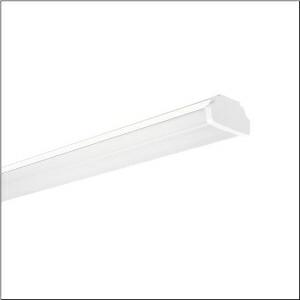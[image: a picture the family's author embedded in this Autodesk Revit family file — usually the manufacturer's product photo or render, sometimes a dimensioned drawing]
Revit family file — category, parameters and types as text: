
# Revit family: modario_r__31_ho_53bm812d2v4120_42ed
name_source: partatom
category: Lighting Fixtures
units: mm (PartAtom-declared; Revit-internal decimal feet)

## family parameters
Cut with Voids When Loaded = No
Host = Face
Light Source = No
Part Type = Normal
Room Calculation Point = No
Round Connector Dimension = Use Diameter
Shared = No

## types (1)
- --- (1 x LED, 12350 lm, 79.5 W, 4000K)
    Apparent Load = 80 VA
    CIE Flux Codes = 47 80 95 92 100
    Color Rendering = 80
    Color Temperature = 4000K
    Default Elevation = 1800 mm
    Description = Modario® 31 HO, luminaire insert, of sheet steel, coil coated, white, length: 1.495mm, width: 81mm, height: 82mm, 5x system unit, system units: 299mm, LED rated luminous flux: 12.350lm, light colour: 840, control gear: DALI 2, control gear: ECG DALI, with plug, 5-pole, with phase selection, mains connection: 220..240V, AC, 50/60Hz, rated input power: 80W, through-wiring accessed according to module size, primary optical cover: cover, of PMMA, light emission: direct distribution, primary light characteristic: symmetric, protection rating (complete): IP20, protection rating (LED compartment): IP50, insulation class (complete): insulation class I (protective earthing), certification: CE, ENEC, VDE, UKCA, impact resistance: IK03, permissible ambient temperature for indoor applications: -25..+30°C, corresponds to IFS (International Featured Standards) requirements for safety and quality in the food industry, reducing of maximum allowable ambient temperature of 5°C with ceiling mounting, packaging unit: 1 piece
    Height = 92 mm
    Lamp = 1 x LED
    Lamp Light Flux = 12350 lm
    Lamp Power = 79.5 W
    Lamp count = 1
    Length = 1495 mm
    Luminous efficacy = 155 lm/W
    Manufacturer = Siteco
    ModVariant = No
    Model = 53BM812D2V4120
    Mounting Place = Ceiling
    Mounting Type = Pendant
    Number of Poles = 1
    OnlyDefault = Yes
    Power Factor = 1
    Product Name = Modario® 31 HO
    Product group = luminaire insert
    ProductGroupID = 902
    Protection Class = Protection class I
    Protection Degree = IP 20
    RLX_Detail_Level = 1
    RLX_Emergency_Light_Flux = 0 lm
    RLX_Emergency_Type = 0
    RLX_Emergency_Type_DB = No
    RlxData = <blob elided: 42261 chars, md5=d68db8b3>
    Socket = socket
    Standby Power = 0 W
    System Light Flux = 12350 lm
    System Power = 80 W
    Type Comments = factory setting: luminous flux: 100 % | dim-lin: 254 | 345 mA
    Type Image = l_1341886.jpg
    URL = http://relux.com
    VarID = @adj_199280
    Voltage = 0 V
    Weight = 0.00 kg
    Width = 81 mm

## geometry (parser evidence)
native form markers: Blend x4, Sweep x12
no freeform markers — native parametric forms only
